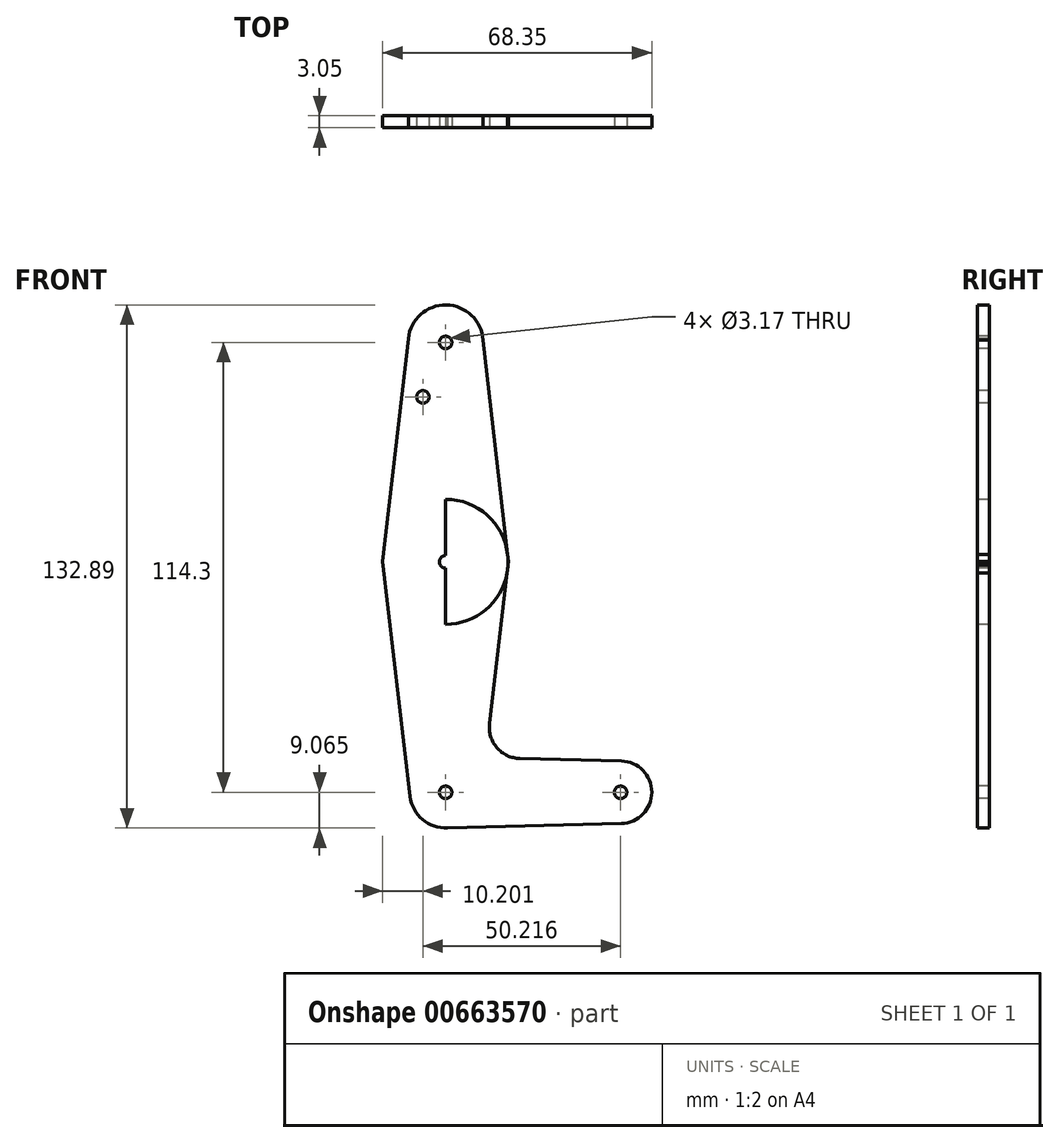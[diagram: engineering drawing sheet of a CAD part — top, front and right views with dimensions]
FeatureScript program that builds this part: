
annotation { "Feature Type Name" : "Feature", "Feature Type Description" : "" }
export const myFeature = defineFeature(function(context is Context, id is Id, definition is map)
    precondition{}
    {
        {
            var Q0;
            Q0=qCreatedBy(makeId("Front.planeOp"),FACE);
            var sketch = newSketch(context, id + "F0", { "sketchPlane" : qUnion([Q0])});
            skLineSegment(sketch, "E0", {"start": v(-51.95, 55.6) * mm, "end": v(-51.95, -58.7) * mm});
            skLineSegment(sketch, "E1", {"start": v(-51.95, -58.7) * mm, "end": v(-7.5, -58.7) * mm});
            skCircle(sketch, "E2", {"center": v(-51.95, 55.6) * mm, "radius": 9.53 * mm});
            skCircle(sketch, "E3", {"center": v(-7.5, -58.7) * mm, "radius": 7.94 * mm});
            skCircle(sketch, "E4", {"center": v(-51.95, -0.14) * mm, "radius": 15.88 * mm});
            skCircle(sketch, "E5", {"center": v(-51.95, -58.7) * mm, "radius": 9.06 * mm});
            skLineSegment(sketch, "E6", {"start": v(-42.45, 56.2) * mm, "end": v(-36, 0) * mm});
            skLineSegment(sketch, "E7", {"start": v(-61.43, 56.57) * mm, "end": v(-67.92, 0) * mm});
            skLineSegment(sketch, "E8", {"start": v(-67.92, 0) * mm, "end": v(-60.95, -59.74) * mm});
            skLineSegment(sketch, "E9", {"start": v(-36, 0) * mm, "end": v(-40.8, -41.24) * mm});
            skLineSegment(sketch, "E10", {"start": v(-33.1, -50.1) * mm, "end": v(-7.3, -50.76) * mm});
            skLineSegment(sketch, "E11", {"start": v(-51.48, -67.74) * mm, "end": v(-7.3, -66.63) * mm});
            skCircle(sketch, "E12", {"center": v(-57.72, 41.78) * mm, "radius": 1.59 * mm});
            skCircle(sketch, "E13", {"center": v(-51.95, -0.14) * mm, "radius": 1.59 * mm});
            skCircle(sketch, "E14", {"center": v(-51.95, 55.6) * mm, "radius": 1.59 * mm});
            skCircle(sketch, "E15", {"center": v(-51.95, -58.7) * mm, "radius": 1.59 * mm});
            skCircle(sketch, "E16", {"center": v(-7.5, -58.7) * mm, "radius": 1.59 * mm});
            skArc(sketch, "E17.filletArc", {"start": v(-40.8, -41.24) * mm, "mid": v(-38.9, -47.37) * mm, "end": v(-33.1, -50.1) * mm});
            skSolve(sketch);
        }
        {
            var Q0;
            {var subQ0=sQuery(id+"F0.wireOp",EDGE,"E7");var subQ1=sQuery(id+"F0.wireOp",EDGE,"E4");var subQ2=makeQuery(id+"F0.imprint","INTERSECT",VERTEX,{"derivedFrom":[subQ1,subQ0]});Q0=makeQuery(id+"F0.imprint","IMPRINT",FACE,{"disambiguationData":[TD([[makeQuery(id+"F0.imprint","IMPRINT",EDGE,{"disambiguationData":[TD([[subQ2,-1.0]])],"derivedFrom":subQ1}),-1.0]])]});}
            var Q1;
            {var subQ0=sQuery(id+"F0.wireOp",EDGE,"E8");var subQ1=sQuery(id+"F0.wireOp",EDGE,"E4");var subQ2=makeQuery(id+"F0.imprint","INTERSECT",VERTEX,{"disambiguationData":[OD(0.0)],"derivedFrom":[subQ1,subQ0]});Q1=makeQuery(id+"F0.imprint","IMPRINT",FACE,{"disambiguationData":[TD([[makeQuery(id+"F0.imprint","IMPRINT",EDGE,{"disambiguationData":[TD([[subQ2,-1.0]])],"derivedFrom":subQ1}),1.0]])]});}
            var Q2;
            {var subQ0=sQuery(id+"F0.wireOp",EDGE,"E9");var subQ1=sQuery(id+"F0.wireOp",EDGE,"E4");var subQ2=makeQuery(id+"F0.imprint","INTERSECT",VERTEX,{"disambiguationData":[OD(0.0)],"derivedFrom":[subQ1,subQ0]});Q2=makeQuery(id+"F0.imprint","IMPRINT",FACE,{"disambiguationData":[TD([[makeQuery(id+"F0.imprint","IMPRINT",EDGE,{"disambiguationData":[TD([[subQ2,-1.0]])],"derivedFrom":subQ1}),1.0]])]});}
            var Q3;
            {var subQ0=sQuery(id+"F0.wireOp",EDGE,"E6");var subQ1=sQuery(id+"F0.wireOp",EDGE,"E4");var subQ2=makeQuery(id+"F0.imprint","INTERSECT",VERTEX,{"derivedFrom":[subQ1,subQ0]});Q3=makeQuery(id+"F0.imprint","IMPRINT",FACE,{"disambiguationData":[TD([[makeQuery(id+"F0.imprint","IMPRINT",EDGE,{"disambiguationData":[TD([[subQ2,1.0]])],"derivedFrom":subQ1}),-1.0]])]});}
            var Q4;
            {var subQ0=sQuery(id+"F0.wireOp",EDGE,"E2");var subQ1=sQuery(id+"F0.wireOp",EDGE,"E0");var subQ2=makeQuery(id+"F0.imprint","INTERSECT",VERTEX,{"derivedFrom":[subQ1,subQ0]});Q4=makeQuery(id+"F0.imprint","IMPRINT",FACE,{"disambiguationData":[TD([[makeQuery(id+"F0.imprint","IMPRINT",EDGE,{"disambiguationData":[TD([[subQ2,-1.0]])],"derivedFrom":subQ1}),1.0]])]});}
            var Q5;
            {var subQ0=sQuery(id+"F0.wireOp",EDGE,"E4");var subQ1=sQuery(id+"F0.wireOp",EDGE,"E0");var subQ2=makeQuery(id+"F0.imprint","INTERSECT",VERTEX,{"disambiguationData":[OD(1.0)],"derivedFrom":[subQ1,subQ0]});Q5=makeQuery(id+"F0.imprint","IMPRINT",FACE,{"disambiguationData":[TD([[makeQuery(id+"F0.imprint","IMPRINT",EDGE,{"disambiguationData":[TD([[subQ2,-1.0]])],"derivedFrom":subQ1}),-1.0]])]});}
            var Q6;
            {var subQ5=sQuery(id+"F0.wireOp",EDGE,"E11");Q6=makeQuery(id+"F0.imprint","IMPRINT",FACE,{"disambiguationData":[TD([[makeQuery(id+"F0.imprint","IMPRINT",EDGE,{"derivedFrom":subQ5}),1.0]])]});}
            var Q7;
            Q7=makeQuery(id+"F0.imprint","IMPRINT",FACE,{"disambiguationData":[TD([[makeQuery(id+"F0.imprint","IMPRINT",EDGE,{"derivedFrom":sQuery(id+"F0.wireOp",EDGE,"E14")}),-1.0]])]});
            var Q8;
            Q8=makeQuery(id+"F0.imprint","IMPRINT",FACE,{"disambiguationData":[TD([[makeQuery(id+"F0.imprint","IMPRINT",EDGE,{"derivedFrom":sQuery(id+"F0.wireOp",EDGE,"E16")}),-1.0]])]});
            var Q9;
            Q9=makeQuery(id+"F0.imprint","IMPRINT",FACE,{"disambiguationData":[TD([[makeQuery(id+"F0.imprint","IMPRINT",EDGE,{"derivedFrom":sQuery(id+"F0.wireOp",EDGE,"E12")}),-1.0]])]});
            var Q10;
            {var subQ0=sQuery(id+"F0.wireOp",EDGE,"E5");var subQ7=sQuery(id+"F0.wireOp",EDGE,"E0");var subQ8=makeQuery(id+"F0.imprint","INTERSECT",VERTEX,{"derivedFrom":[subQ7,subQ0]});Q10=makeQuery(id+"F0.imprint","IMPRINT",FACE,{"disambiguationData":[TD([[makeQuery(id+"F0.imprint","IMPRINT",EDGE,{"disambiguationData":[TD([[subQ8,-1.0]])],"derivedFrom":subQ7}),-1.0]])]});}
            var Q11;
            {var subQ5=sQuery(id+"F0.wireOp",EDGE,"E10");Q11=makeQuery(id+"F0.imprint","IMPRINT",FACE,{"disambiguationData":[TD([[makeQuery(id+"F0.imprint","IMPRINT",EDGE,{"derivedFrom":subQ5}),-1.0]])]});}
            var Q12;
            {var subQ1=sQuery(id+"F0.wireOp",EDGE,"E0");var subQ3=sQuery(id+"F0.wireOp",EDGE,"E4");var subQ9=makeQuery(id+"F0.imprint","INTERSECT",VERTEX,{"disambiguationData":[OD(0.0)],"derivedFrom":[subQ1,subQ3]});Q12=makeQuery(id+"F0.imprint","IMPRINT",FACE,{"disambiguationData":[TD([[makeQuery(id+"F0.imprint","IMPRINT",EDGE,{"disambiguationData":[TD([[subQ9,-1.0]])],"derivedFrom":subQ1}),1.0]])]});}
            var Q13;
            {var subQ0=sQuery(id+"F0.wireOp",EDGE,"E4");var subQ2=sQuery(id+"F0.wireOp",EDGE,"E0");var subQ3=makeQuery(id+"F0.imprint","INTERSECT",VERTEX,{"disambiguationData":[OD(0.0)],"derivedFrom":[subQ2,subQ0]});Q13=makeQuery(id+"F0.imprint","IMPRINT",FACE,{"disambiguationData":[TD([[makeQuery(id+"F0.imprint","IMPRINT",EDGE,{"disambiguationData":[TD([[subQ3,-1.0]])],"derivedFrom":subQ2}),-1.0]])]});}
            var Q14;
            {var subQ0=sQuery(id+"F0.wireOp",EDGE,"E5");var subQ1=sQuery(id+"F0.wireOp",EDGE,"E0");var subQ2=makeQuery(id+"F0.imprint","INTERSECT",VERTEX,{"derivedFrom":[subQ1,subQ0]});Q14=makeQuery(id+"F0.imprint","IMPRINT",FACE,{"disambiguationData":[TD([[makeQuery(id+"F0.imprint","IMPRINT",EDGE,{"disambiguationData":[TD([[subQ2,-1.0]])],"derivedFrom":subQ1}),1.0]])]});}
            extrude(context, id + "F1", {"entities" : qUnion([Q0, Q1, Q2, Q3, Q4, Q5, Q6, Q7, Q8, Q9, Q10, Q11, Q12, Q13, Q14]), "oppositeDirection" : true, "depth" : 3.05 * mm, "offsetDistance" : 25.4 * mm});
        }
    });
